FCSTD DOCUMENT  (FreeCAD 0.16R)
Label: beadlock1
License: All rights reserved
LicenseURL: http://en.wikipedia.org/wiki/All_rights_reserved
objects: Sketcher::SketchObject×1
note: 1 computed .brp shape members not serialized (recipe doc carries the construction recipe); baked Part::Feature solids carry a one-line shape summary decoded from their .brp

FEATURE [Sketcher::SketchObject] Sketch
  sketch-geometry (16):
    g0: LineSegment StartX=-38.8 StartY=0 StartZ=0 EndX=-38.8 EndY=-0.4 EndZ=0
    g1: LineSegment StartX=-38.8 StartY=-0.4 StartZ=0 EndX=-31.3 EndY=-0.4 EndZ=0
    g2: LineSegment StartX=-31.3 StartY=-0.4 StartZ=0 EndX=-31.3 EndY=-4.8 EndZ=0
    g3: LineSegment StartX=-31.3 StartY=-4.8 StartZ=0 EndX=-22.8 EndY=-4.8 EndZ=0
    g4: LineSegment StartX=-22.8 StartY=-4.8 StartZ=0 EndX=-22.8 EndY=-8 EndZ=0
    g5: LineSegment StartX=-22.8 StartY=-8 StartZ=0 EndX=-8.8 EndY=-8 EndZ=0
    g6: LineSegment StartX=-8.8 StartY=-8 StartZ=0 EndX=-8.8 EndY=-9 EndZ=0
    g7: LineSegment StartX=8.8 StartY=-9 StartZ=0 EndX=8.8 EndY=-8 EndZ=0
    g8: LineSegment StartX=8.8 StartY=-8 StartZ=0 EndX=22.8 EndY=-8 EndZ=0
    g9: LineSegment StartX=22.8 StartY=-8 StartZ=0 EndX=22.8 EndY=-4.8 EndZ=0
    g10: LineSegment StartX=22.8 StartY=-4.8 StartZ=0 EndX=31.3 EndY=-4.8 EndZ=0
    g11: LineSegment StartX=31.3 StartY=-4.8 StartZ=0 EndX=31.3 EndY=-0.4 EndZ=0
    g12: LineSegment StartX=31.3 StartY=-0.4 StartZ=0 EndX=38.8 EndY=-0.4 EndZ=0
    g13: LineSegment StartX=38.8 StartY=-0.4 StartZ=0 EndX=38.8 EndY=0 EndZ=0
    g14: LineSegment StartX=-8.8 StartY=-9 StartZ=0 EndX=8.8 EndY=-9 EndZ=0
    g15: LineSegment StartX=-38.8 StartY=0 StartZ=0 EndX=38.8 EndY=0 EndZ=0
  constraints (48):
    c: PointOnObject(g0,g-1)
    c: Coincident(g0,g1)
    c: Horizontal(g1)
    c: Coincident(g1,g2)
    c: Coincident(g2,g3)
    c: Horizontal(g3)
    c: Coincident(g3,g4)
    c: Coincident(g4,g5)
    c: Horizontal(g5)
    c: Coincident(g5,g6)
    c: Vertical(g6)
    c: Coincident(g7,g8)
    c: Horizontal(g8)
    c: Coincident(g8,g9)
    c: Coincident(g9,g10)
    c: Horizontal(g10)
    c: Coincident(g10,g11)
    c: Coincident(g11,g12)
    c: Horizontal(g12)
    c: Coincident(g12,g13)
    c: Symmetric(g0,g13,g-1)
    c: Vertical(g0)
    c: Vertical(g2)
    c: Vertical(g4)
    c: Vertical(g7)
    c: Vertical(g9)
    c: Vertical(g13)
    c: Equal(g0,g13)
    c: DistanceY(g0,g0) = 0.4
    c: Equal(g2,g11)
    c: Vertical(g11)
    c: DistanceY(g11,g11) = 4.4
    c: Equal(g9,g4)
    c: DistanceY(g9,g9) = 3.2
    c: Equal(g7,g6)
    c: DistanceY(g7,g7) = 1
    c: Symmetric(g1,g11,g-2)
    c: Symmetric(g9,g3,g-2)
    c: Symmetric(g7,g5,g-2)
    c: DistanceX(g1,g1) = 7.5
    c: DistanceX(g3,g3) = 8.5
    c: DistanceX(g5,g5) = 14
    c: DistanceX(g12) = 38.8
    c: Coincident(g14,g6)
    c: Horizontal(g14)
    c: Coincident(g15,g0)
    c: Coincident(g15,g13)
    c: Horizontal(g15)
